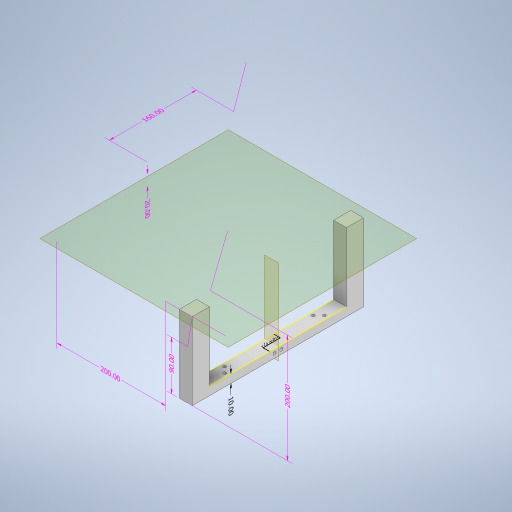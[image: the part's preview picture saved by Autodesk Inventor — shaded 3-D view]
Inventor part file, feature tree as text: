
AUTODESK INVENTOR PART (.ipt)
format: ipt  version: 2023 (Build 270158000, 158)  size: 384,000 bytes
history: native  units: mm
features: sketch x9, other x8, extrude x5, hole x3, plane x2, split x1
ambient origin geometry x8: Origin, YZ Plane, XZ Plane, XY Plane, X Axis, Y Axis, Z Axis, Center Point
bodies: Body1 (feature_tree)
feature tree (28):
  other  "Sólido1"
  other  "Anotaciones"
  extrude  "Extrusión1"  Depth=200.0mm
  hole  "Agujero1"  [1 undecoded]
  extrude  "Extrusión2"  Depth=15.0mm
  extrude  "Extrusión3"  Depth=80.0mm TaperAngle=0.0deg
  extrude  "Extrusión4"  Depth=200.0mm
  extrude  "Extrusión5"  Depth=20.0mm
  hole  "Agujero2"  [1 undecoded]
  plane  "Plano de trabajo1"
  split  "Dividir1"
  plane  "Plano de trabajo2"
  hole  "Agujero3"  [1 undecoded]
  sketch  "Boceto10"  dims[d39=90.0mm d40=0.0mm d43=30.0mm d44=0.0mm d45=3.5mm d46=1.75mm d47=1.75mm d48=1.75mm d49=1.75mm d50=10.0mm d51=10.0mm d52=15.0mm d53=10.0mm d54=10.0mm d55=15.0mm d56=3.5mm d57=6.0mm d58=4.0mm d59=2.0mm d60=90.0deg d61=8.0mm d62=20.594885mm d63=10.0mm d65=10.0mm d75=200.0mm d76=10.0mm d77=20.0mm d81=40.0mm d88=90.0deg d89=3.5mm d90=3.5mm d91=6.0mm d92=4.0mm d93=2.0mm d94=90.0deg d95=8.0mm d96=20.594885mm d97=10.0mm d98=10.0mm d66=5.760865mm d67=7.72461mm d68=200.0mm d69=3.008686mm d70=2.422102mm d71=10.0mm d72=3.500509mm d73=2.402572mm d74=90.0mm d78=3.13122mm d79=6.269346mm d80=200.0mm d82=8.450127mm d83=0.968417mm d84=20.0mm d85=4.759975mm d86=4.646891mm d87=160.0mm]
  sketch  "Boceto2"  dims[d7=15.0mm d8=200.0mm]
  sketch  "Boceto3"  dims[d9=10.0mm d10=0.0mm]
  sketch  "Boceto4"  dims[d11=3.5mm d12=1.75mm d13=1.75mm d14=1.75mm d15=1.75mm d16=10.0mm d17=10.0mm d19=40.0mm]
  sketch  "Boceto5"  dims[d20=3.5mm d21=6.0mm d22=4.0mm d23=2.0mm d24=90.0deg d25=8.0mm d26=20.594885mm d27=15.0mm]
  sketch  "Boceto6"  dims[d28=20.0mm d29=80.0mm d30=0.0mm]
  sketch  "Boceto7"  dims[d31=57.0mm d32=200.0mm]
  sketch  "Boceto8"  dims[d33=110.0mm d34=0.0mm d36=20.0mm]
  sketch  "Boceto9"  dims[d37=20.0mm d38=20.0mm]
  other  "Cota lineal 1"
  other  "Cota lineal 2"
  other  "Cota lineal 3"
  other  "Cota lineal 4"
  other  "Cota lineal 5"
  other  "Cota lineal 6"
note: 3 required parameter values undecoded (feature->parameter linkage not recoverable at this tier; creation-order binding heuristic only, values carry confidence <= 0.55)
